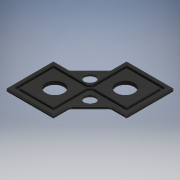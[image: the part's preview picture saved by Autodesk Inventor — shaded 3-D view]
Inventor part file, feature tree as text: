
AUTODESK INVENTOR PART (.ipt)
format: ipt  version: 2018 (Build 220112000, 112)  size: 887,808 bytes
history: native  units: mm
features: other x2, extrude x1, sketch x1
ambient origin geometry x8: Origin, YZ Plane, XZ Plane, XY Plane, X Axis, Y Axis, Z Axis, Center Point
bodies: Solid1 (feature_tree)
feature tree (4):
  other  "28mm_Parasitic_Element"
  other  "MeshFeature1"
  extrude  "Extrusion1"  Depth=2.62mm
  sketch  "Sketch1"  dims[d0=13.0mm d1=13.0mm d2=22.0mm d3=22.0mm d4=2.62mm d5=0.0mm]
